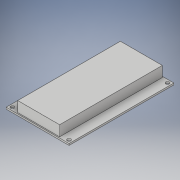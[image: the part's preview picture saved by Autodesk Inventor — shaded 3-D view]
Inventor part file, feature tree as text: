
AUTODESK INVENTOR PART (.ipt)
format: ipt  version: 2019 (Build 230136000, 136)  size: 120,832 bytes
history: native  units: mm
features: sketch x3, extrude x2, hole x1, plane x1
ambient origin geometry x8: Origin, YZ Plane, XZ Plane, XY Plane, X Axis, Y Axis, Z Axis, Center Point
bodies: Solid1 (feature_tree)
feature tree (7):
  extrude  "Extrusion1"  Depth=100.0mm
  hole  "Hole1"  [1 undecoded]
  extrude  "Extrusion2"  Depth=10.0mm
  plane  "Work Plane1"
  sketch  "Sketch1"  dims[d0=60.0mm d1=100.0mm]
  sketch  "Sketch2"  dims[d2=1.6mm d3=0.0mm d4=3.0mm]
  sketch  "Sketch3"  dims[d5=3.0mm d6=20.0mm d8=54.0mm d9=20.0mm d11=94.0mm d14=3.4mm d15=6.0mm d16=6.3mm d17=2.0mm d18=90.0deg d19=8.0mm d20=20.594885mm d21=40.0mm d22=98.0mm d23=10.0mm d24=0.0mm]
note: 1 required parameter value undecoded (feature->parameter linkage not recoverable at this tier; creation-order binding heuristic only, values carry confidence <= 0.55)
